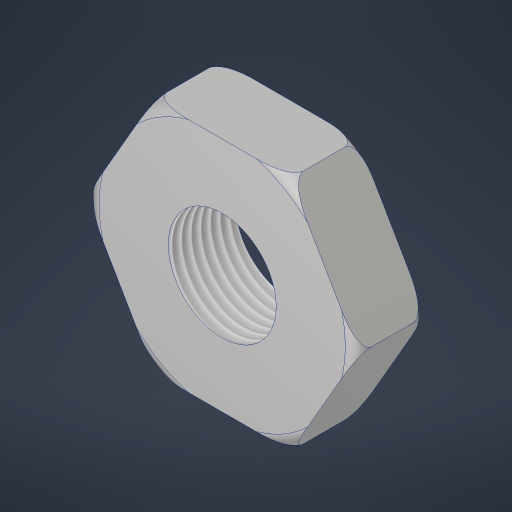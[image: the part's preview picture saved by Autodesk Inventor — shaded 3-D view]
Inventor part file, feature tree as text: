
AUTODESK INVENTOR PART (.ipt)
format: ipt  version: 2023.4 (Build 274418000, 418)  size: 239,616 bytes
history: native  units: in
note: dims shown in document units (in); Inventor stores cm internally (conversion verified against a paired STEP export)
features: sketch x3, extrude x1, hole x1, revolve x1, projected_geometry x1
ambient origin geometry x8: Origin, YZ Plane, XZ Plane, XY Plane, X Axis, Y Axis, Z Axis, Center Point
bodies: Solid1 (feature_tree)
feature tree (7):
  extrude  "Extrusion1"  Depth=0.5in TaperAngle=0.0deg
  hole  "Hole1"  [1 undecoded]
  revolve  "Revolution1"  [1 undecoded]
  sketch  "Sketch1"  dims[d1=1.75in d2=0.5in d3=0.0in]
  sketch  "Sketch2"  dims[d4=0.798in d5=1.75in d6=0.375in d7=0.25in d8=0.5635in d9=1.0in d10=0.8108in d11=0.1in]
  sketch  "Sketch3"  dims[d12=0.1in d13=0.1in d14=90.0deg]
  projected_geometry  "Project Cut Edges1"
note: 2 required parameter values undecoded (feature->parameter linkage not recoverable at this tier; creation-order binding heuristic only, values carry confidence <= 0.55)